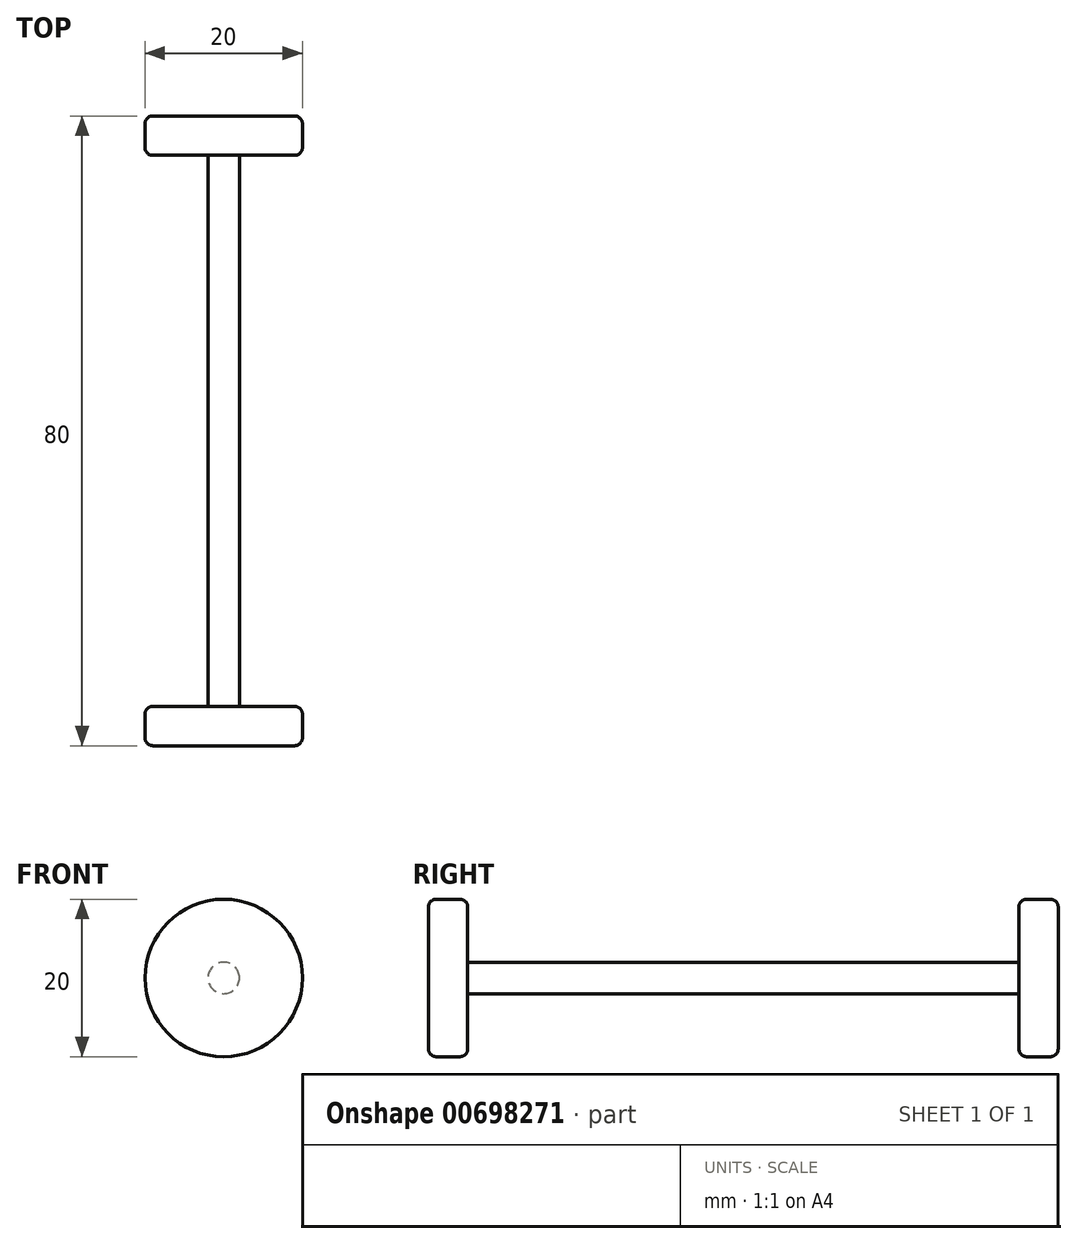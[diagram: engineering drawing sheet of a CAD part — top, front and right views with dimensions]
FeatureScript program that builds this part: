
annotation { "Feature Type Name" : "Feature", "Feature Type Description" : "" }
export const myFeature = defineFeature(function(context is Context, id is Id, definition is map)
    precondition{}
    {
        {
            var Q0;
            Q0=qCreatedBy(makeId("Front.planeOp"),FACE);
            var sketch = newSketch(context, id + "F0", { "sketchPlane" : qUnion([Q0])});
            skCircle(sketch, "E0", {"center": v(0, 0) * mm, "radius": 2 * mm});
            skSolve(sketch);
        }
        {
            var Q0;
            Q0=makeQuery(id+"F0.imprint","IMPRINT",FACE,{"disambiguationData":[TD([[makeQuery(id+"F0.imprint","IMPRINT",EDGE,{"derivedFrom":sQuery(id+"F0.wireOp",EDGE,"E0")}),1.0]])]});
            var Q1;
            Q1 = qSketchRegion(id + "F2", true);
            extrude(context, id + "F1", {"entities" : qUnion([Q0, Q1]), "depth" : 70 * mm, "offsetDistance" : 25 * mm});
        }
        {
            var Q0;
            Q0=makeQuery(id+"F1.opExtrude","CAP_FACE",FACE,{"disambiguationData":[OSD([sQuery(id+"F0.wireOp",EDGE,"E0")])],"isStart":false});
            var sketch = newSketch(context, id + "F2", { "sketchPlane" : qUnion([Q0])});
            skCircle(sketch, "E1", {"center": v(0, 0) * mm, "radius": 10 * mm});
            skSolve(sketch);
        }
        {
            var Q0;
            Q0 = qSketchRegion(id + "F2", true);
            extrude(context, id + "F3", {"entities" : qUnion([Q0]), "operationType" : NewBodyOperationType.ADD, "depth" : 5 * mm, "offsetDistance" : 25 * mm});
        }
        {
            var Q0;
            Q0=makeQuery(id+"F3.opExtrude","CAP_EDGE",EDGE,{"disambiguationData":[OSD([sQuery(id+"F2.wireOp",EDGE,"E1")])],"isStart":true});
            var Q1;
            Q1=makeQuery(id+"F3.opExtrude","CAP_EDGE",EDGE,{"disambiguationData":[OSD([sQuery(id+"F2.wireOp",EDGE,"E1")])],"isStart":false});
            fillet(context, id + "F4", {"entities" : qUnion([Q0, Q1]), "radius" : 1 * mm, "tangentPropagation" : true, "allowEdgeOverflow" : false});
        }
        {
            var Q0;
            Q0=makeQuery(id+"F1.opExtrude","CAP_FACE",FACE,{"disambiguationData":[OSD([sQuery(id+"F0.wireOp",EDGE,"E0")])],"isStart":true});
            var sketch = newSketch(context, id + "F5", { "sketchPlane" : qUnion([Q0])});
            skCircle(sketch, "E2", {"center": v(0, 0) * mm, "radius": 10 * mm});
            skSolve(sketch);
        }
        {
            var Q0;
            Q0=makeQuery(id+"F5.imprint","IMPRINT",FACE,{"disambiguationData":[TD([[makeQuery(id+"F5.imprint","IMPRINT",EDGE,{"derivedFrom":sQuery(id+"F5.wireOp",EDGE,"E2")}),1.0]])]});
            var Q1;
            Q1=makeQuery(id+"F5.imprint","IMPRINT",FACE,{"disambiguationData":[TD([[makeQuery(id+"F5.imprint","IMPRINT",EDGE,{"derivedFrom":makeQuery(id+"F1.opExtrude","CAP_EDGE",EDGE,{"disambiguationData":[OSD([sQuery(id+"F0.wireOp",EDGE,"E0")])],"isStart":true})}),-1.0]])]});
            extrude(context, id + "F6", {"entities" : qUnion([Q0, Q1]), "operationType" : NewBodyOperationType.ADD, "depth" : 5 * mm, "offsetDistance" : 25 * mm});
        }
        {
            var Q0;
            Q0=makeQuery(id+"F6.opExtrude","CAP_EDGE",EDGE,{"disambiguationData":[OSD([sQuery(id+"F5.wireOp",EDGE,"E2")])],"isStart":true});
            var Q1;
            Q1=makeQuery(id+"F6.opExtrude","CAP_EDGE",EDGE,{"disambiguationData":[OSD([sQuery(id+"F5.wireOp",EDGE,"E2")])],"isStart":false});
            fillet(context, id + "F7", {"entities" : qUnion([Q0, Q1]), "radius" : 1 * mm, "tangentPropagation" : true, "allowEdgeOverflow" : false});
        }
    });
